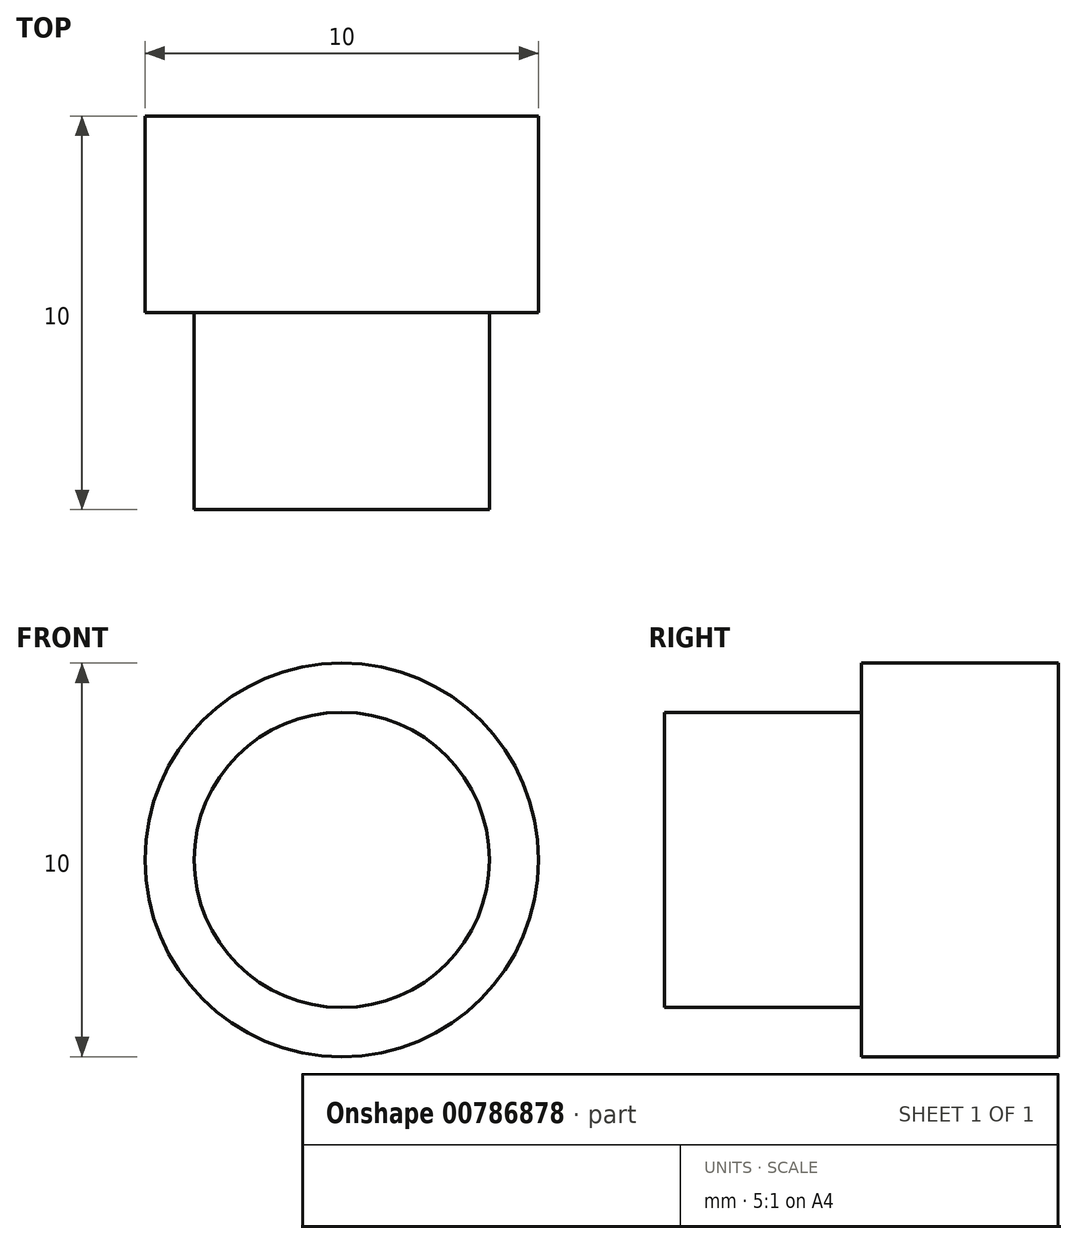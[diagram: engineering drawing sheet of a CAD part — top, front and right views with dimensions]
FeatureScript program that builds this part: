
annotation { "Feature Type Name" : "Feature", "Feature Type Description" : "" }
export const myFeature = defineFeature(function(context is Context, id is Id, definition is map)
    precondition{}
    {
        {
            var Q0;
            Q0=qCreatedBy(makeId("Front.planeOp"),FACE);
            var sketch = newSketch(context, id + "F0", { "sketchPlane" : qUnion([Q0])});
            skCircle(sketch, "E0", {"center": v(0, 0) * mm, "radius": 5 * mm});
            skCircle(sketch, "E1", {"center": v(0, 0) * mm, "radius": 3.75 * mm});
            skSolve(sketch);
        }
        {
            var Q0;
            Q0=makeQuery(id+"F0.imprint","IMPRINT",FACE,{"disambiguationData":[TD([[makeQuery(id+"F0.imprint","IMPRINT",EDGE,{"derivedFrom":sQuery(id+"F0.wireOp",EDGE,"E1")}),1.0]])]});
            extrude(context, id + "F1", {"entities" : qUnion([Q0]), "depth" : 5 * mm, "offsetDistance" : 25 * mm});
        }
        {
            var Q0;
            Q0=makeQuery(id+"F0.imprint","IMPRINT",FACE,{"disambiguationData":[TD([[makeQuery(id+"F0.imprint","IMPRINT",EDGE,{"derivedFrom":sQuery(id+"F0.wireOp",EDGE,"E0")}),1.0]])]});
            var Q1;
            Q1=makeQuery(id+"F0.imprint","IMPRINT",FACE,{"disambiguationData":[TD([[makeQuery(id+"F0.imprint","IMPRINT",EDGE,{"derivedFrom":sQuery(id+"F0.wireOp",EDGE,"E1")}),1.0]])]});
            extrude(context, id + "F2", {"entities" : qUnion([Q0, Q1]), "operationType" : NewBodyOperationType.ADD, "oppositeDirection" : true, "depth" : 5 * mm, "offsetDistance" : 25 * mm});
        }
    });
